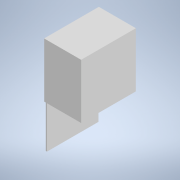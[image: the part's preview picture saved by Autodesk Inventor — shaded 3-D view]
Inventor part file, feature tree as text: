
AUTODESK INVENTOR PART (.ipt)
format: ipt  version: 2022 (Build 260153000, 153)  size: 123,904 bytes
history: native  units: mm
features: extrude x2, sketch x2, other x1
ambient origin geometry x8: Origin, YZ Plane, XZ Plane, XY Plane, X Axis, Y Axis, Z Axis, Center Point
bodies: Body1 (feature_tree)
feature tree (5):
  other  "Твердое тело1"
  extrude  "Выдавливание1"  Depth=14.0mm
  extrude  "Выдавливание2"  Depth=14.0mm
  sketch  "Эскиз1"
  sketch  "Эскиз2"
